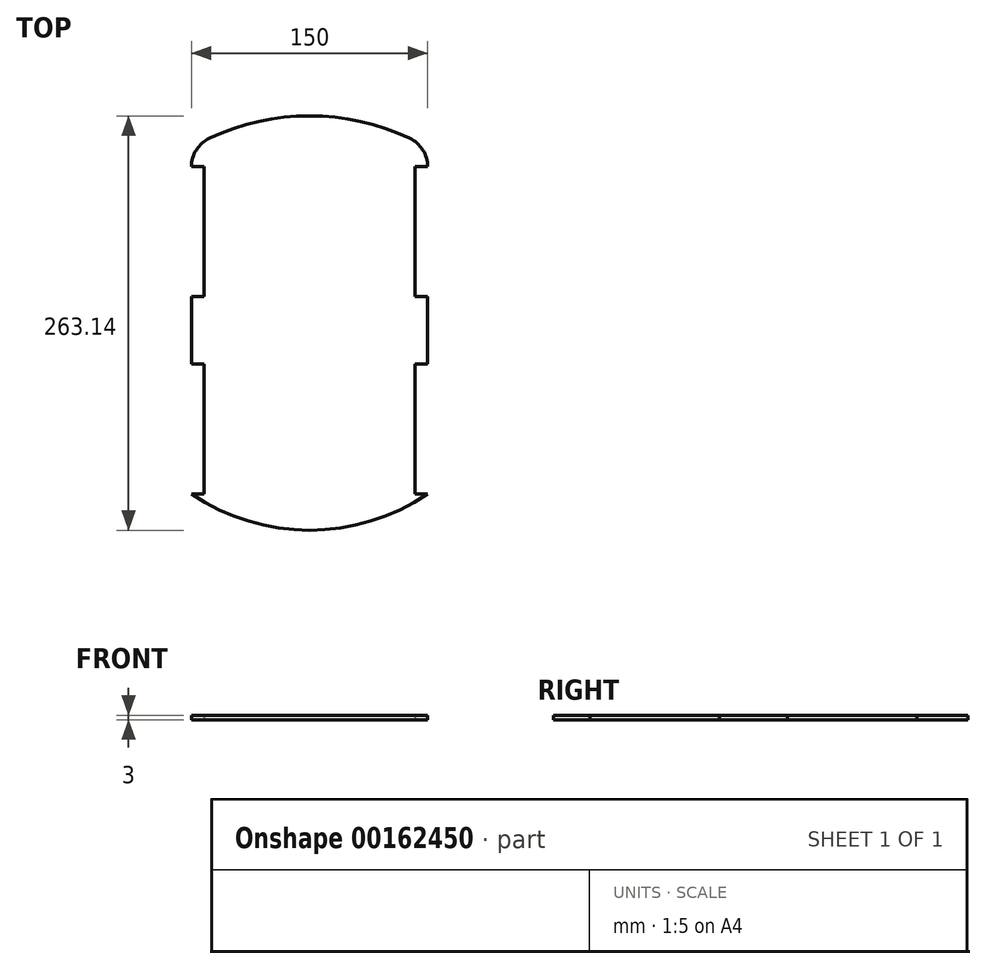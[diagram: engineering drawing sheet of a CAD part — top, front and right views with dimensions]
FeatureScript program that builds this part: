
annotation { "Feature Type Name" : "Feature", "Feature Type Description" : "" }
export const myFeature = defineFeature(function(context is Context, id is Id, definition is map)
    precondition{}
    {
        {
            var Q0;
            Q0=qCreatedBy(makeId("Top.planeOp"),FACE);
            var sketch = newSketch(context, id + "F0", { "sketchPlane" : qUnion([Q0])});
            skLineSegment(sketch, "E0.bottom", {"start": v(75, 110) * mm, "end": v(70.94, 110) * mm});
            skLineSegment(sketch, "E0.top", {"start": v(75, -110) * mm, "end": v(67, -110) * mm});
            skLineSegment(sketch, "E0.left", {"start": v(75, 15.42) * mm, "end": v(75, -27.5) * mm});
            skLineSegment(sketch, "E0.right", {"start": v(-75, 15.42) * mm, "end": v(-75, -27.5) * mm});
            skPoint(sketch, "E0.middle", {"position": v(0, 0) * mm});
            skArc(sketch, "E1", {"start": v(63.5, 116.02) * mm, "mid": v(0, 130.18) * mm, "end": v(-63.5, 116.02) * mm});
            skPoint(sketch, "E2.visualSharp", {"position": v(75, 110) * mm});
            skArc(sketch, "E2.filletArc", {"start": v(75, 97.92) * mm, "mid": v(71.88, 108.64) * mm, "end": v(63.5, 116.02) * mm});
            skPoint(sketch, "E3.visualSharp", {"position": v(-75, 110) * mm});
            skArc(sketch, "E3.filletArc", {"start": v(-63.5, 116.02) * mm, "mid": v(-71.88, 108.64) * mm, "end": v(-75, 97.92) * mm});
            skLineSegment(sketch, "E4.trimOffspring", {"start": v(-70.94, 110) * mm, "end": v(-75, 110) * mm});
            skLineSegment(sketch, "E5", {"start": v(75, 97.92) * mm, "end": v(67, 97.92) * mm});
            skLineSegment(sketch, "E6", {"start": v(67, 97.92) * mm, "end": v(67, 15.42) * mm});
            skLineSegment(sketch, "E7", {"start": v(67, 15.42) * mm, "end": v(75, 15.42) * mm});
            skLineSegment(sketch, "E8", {"start": v(67, -110) * mm, "end": v(67, -27.5) * mm});
            skLineSegment(sketch, "E9", {"start": v(67, -27.5) * mm, "end": v(75, -27.5) * mm});
            skLineSegment(sketch, "E10", {"start": v(-75, -110) * mm, "end": v(-67, -110) * mm});
            skPoint(sketch, "E11.visualSharp", {"position": v(75, -110) * mm});
            skPoint(sketch, "E12.visualSharp", {"position": v(-75, -110) * mm});
            skLineSegment(sketch, "E13", {"start": v(-75, -27.5) * mm, "end": v(-67, -27.5) * mm});
            skPoint(sketch, "E14.start.orphan", {"position": v(-68.98, -97.18) * mm});
            skArc(sketch, "E15", {"start": v(-75, -110) * mm, "mid": v(0, -132.96) * mm, "end": v(75, -110) * mm});
            skLineSegment(sketch, "E16", {"start": v(-67, -27.5) * mm, "end": v(-67, -110) * mm});
            skLineSegment(sketch, "E17.trimOffspring", {"start": v(67, -110) * mm, "end": v(75, -110) * mm});
            skPoint(sketch, "E18.start.orphan", {"position": v(-75, -97.18) * mm});
            skLineSegment(sketch, "E19", {"start": v(-75, 97.92) * mm, "end": v(-67, 97.92) * mm});
            skLineSegment(sketch, "E20", {"start": v(-67, 97.92) * mm, "end": v(-67, 15.42) * mm});
            skLineSegment(sketch, "E21", {"start": v(-67, 15.42) * mm, "end": v(-75, 15.42) * mm});
            skSolve(sketch);
        }
        {
            var Q0;
            Q0=makeQuery(id+"F0.imprint","IMPRINT",FACE,{"disambiguationData":[TD([[makeQuery(id+"F0.imprint","IMPRINT",EDGE,{"derivedFrom":sQuery(id+"F0.wireOp",EDGE,"E0.left")}),-1.0]])]});
            extrude(context, id + "F1", {"entities" : qUnion([Q0]), "depth" : 3 * mm});
        }
    });
